# Revit family: Recirc Kit
name_source: partatom
category: Generic Models
units: mm (PartAtom-declared; Revit-internal decimal feet)

## family parameters
Always vertical = No
Can host rebar = No
Cut with Voids When Loaded = Yes
Part Type = Normal
Room Calculation Point = No
Round Connector Dimension = Use Diameter
Shared = No
Work Plane-Based = Yes

## types (1)
- KRECIRCDDFT
    Cavity - Depth = 440 mm  [stored 1.44357 ft]
    Cavity - Height = 376 mm  [stored 1.2336 ft]
    Cavity - Width = 800 mm  [stored 2.62467 ft]
    Default Elevation = 0 mm  [stored 0 ft]
    Description = Kit Recirculation Downdraft FP US
    Manufacturer = Fisher & Paykel Appliances
    Model = KRECIRCDDFT
    Product - Depth = 289 mm  [stored 0.948163 ft]
    Product - Height = 96 mm  [stored 0.314961 ft]
    Product - Width = 720 mm  [stored 2.3622 ft]
    URL = www.fisherpaykel.com

note: [stored X ft] marks values corroborated as IEEE doubles in the binary element streams (Revit-internal decimal feet)

## geometry (parser evidence)
native form markers: Sweep x115
no freeform markers — native parametric forms only
